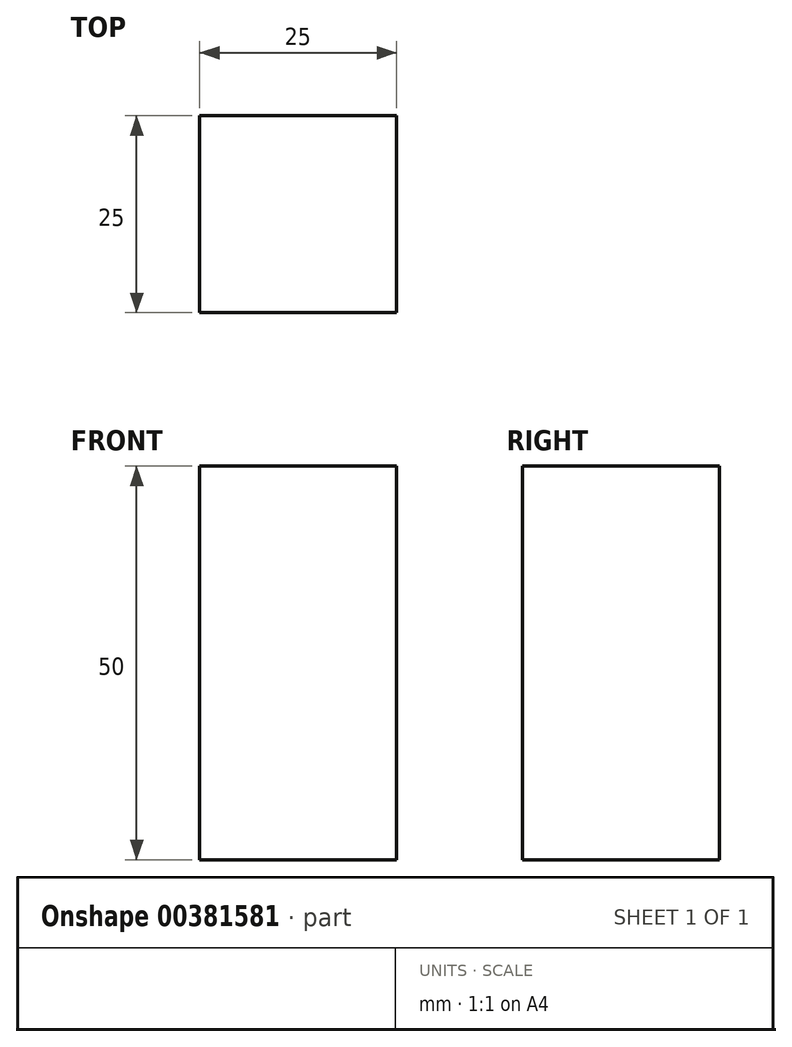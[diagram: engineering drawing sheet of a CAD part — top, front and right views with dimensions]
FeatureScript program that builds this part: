
annotation { "Feature Type Name" : "Feature", "Feature Type Description" : "" }
export const myFeature = defineFeature(function(context is Context, id is Id, definition is map)
    precondition{}
    {
        {
            var Q0;
            Q0=qCreatedBy(makeId("Top.planeOp"),FACE);
            var sketch = newSketch(context, id + "F0", { "sketchPlane" : qUnion([Q0])});
            skLineSegment(sketch, "E0.bottom", {"start": v(12.5, -12.5) * mm, "end": v(-12.5, -12.5) * mm});
            skLineSegment(sketch, "E0.top", {"start": v(12.5, 12.5) * mm, "end": v(-12.5, 12.5) * mm});
            skLineSegment(sketch, "E0.left", {"start": v(12.5, -12.5) * mm, "end": v(12.5, 12.5) * mm});
            skLineSegment(sketch, "E0.right", {"start": v(-12.5, -12.5) * mm, "end": v(-12.5, 12.5) * mm});
            skPoint(sketch, "E0.middle", {"position": v(0, 0) * mm});
            skSolve(sketch);
        }
        {
            var Q0;
            Q0=makeQuery(id+"F0.imprint","IMPRINT",FACE,{"disambiguationData":[TD([[makeQuery(id+"F0.imprint","IMPRINT",EDGE,{"derivedFrom":sQuery(id+"F0.wireOp",EDGE,"E0.bottom")}),-1.0]])]});
            extrude(context, id + "F1", {"entities" : qUnion([Q0]), "depth" : 50 * mm});
        }
    });
